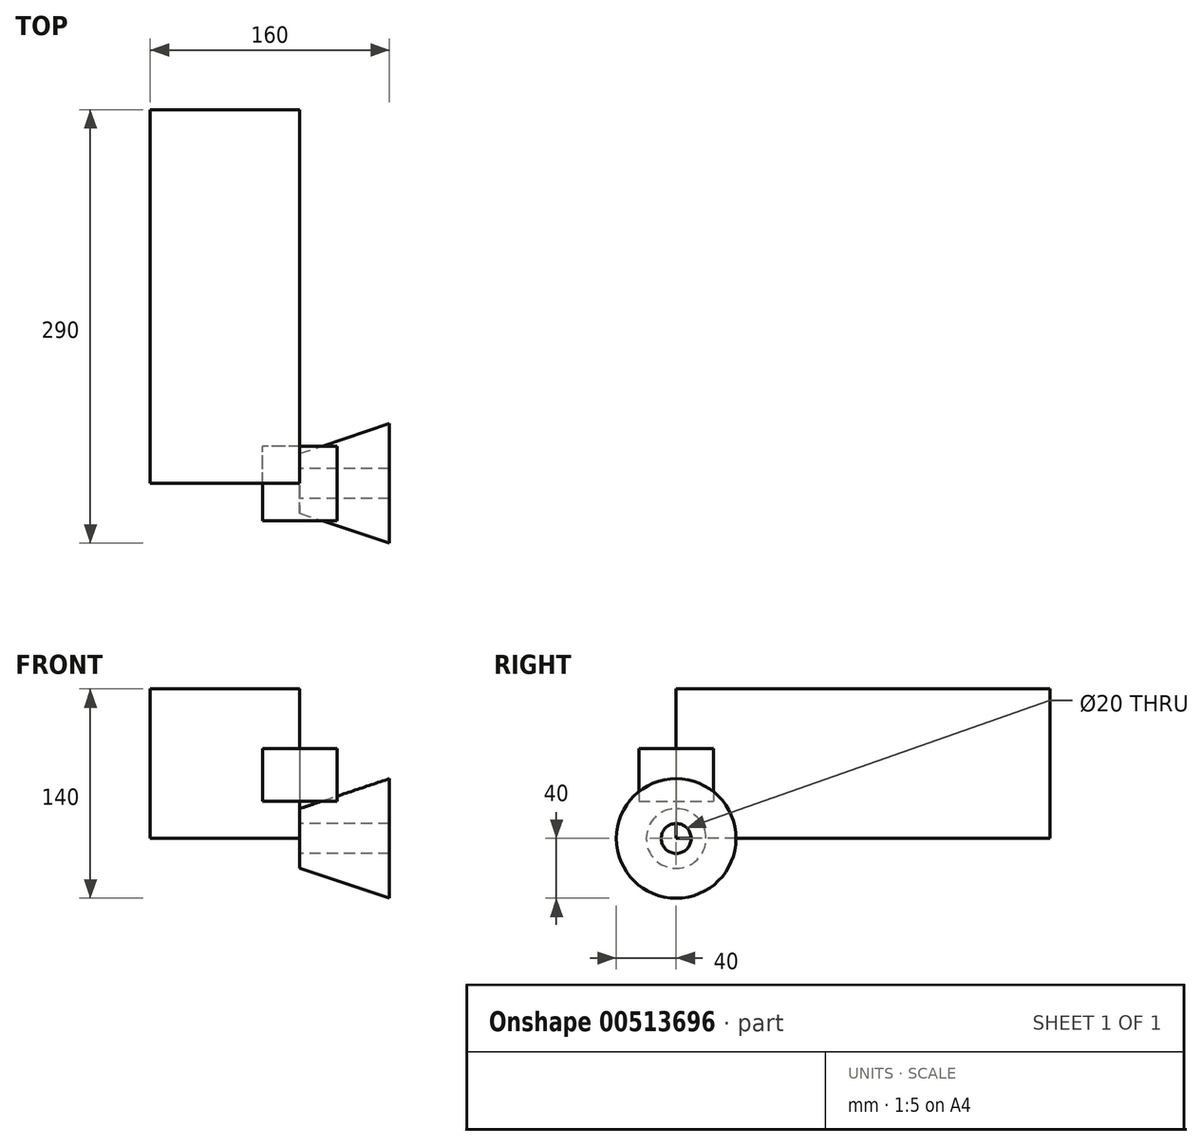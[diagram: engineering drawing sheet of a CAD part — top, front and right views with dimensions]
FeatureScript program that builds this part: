
annotation { "Feature Type Name" : "Feature", "Feature Type Description" : "" }
export const myFeature = defineFeature(function(context is Context, id is Id, definition is map)
    precondition{}
    {
        {
            var Q0;
            Q0=qCreatedBy(makeId("Top.planeOp"),FACE);
            var sketch = newSketch(context, id + "F0", { "sketchPlane" : qUnion([Q0])});
            skLineSegment(sketch, "E0.bottom", {"start": v(0, 250) * mm, "end": v(-100, 250) * mm});
            skLineSegment(sketch, "E0.top", {"start": v(0, 0) * mm, "end": v(-100, 0) * mm});
            skLineSegment(sketch, "E0.left", {"start": v(0, 250) * mm, "end": v(0, 0) * mm});
            skLineSegment(sketch, "E0.right", {"start": v(-100, 250) * mm, "end": v(-100, 0) * mm});
            skSolve(sketch);
        }
        {
            var Q0;
            Q0=makeQuery(id+"F0.imprint","IMPRINT",FACE,{"disambiguationData":[TD([[makeQuery(id+"F0.imprint","IMPRINT",EDGE,{"derivedFrom":sQuery(id+"F0.wireOp",EDGE,"E0.bottom")}),1.0]])]});
            extrude(context, id + "F1", {"entities" : qUnion([Q0]), "depth" : 100 * mm});
        }
        {
            var Q0;
            Q0=qCreatedBy(makeId("Top.planeOp"),FACE);
            var sketch = newSketch(context, id + "F2", { "sketchPlane" : qUnion([Q0])});
            skLineSegment(sketch, "E1", {"start": v(0, 20) * mm, "end": v(60, 40) * mm});
            skLineSegment(sketch, "E2", {"start": v(60, 40) * mm, "end": v(60, 10) * mm});
            skLineSegment(sketch, "E3", {"start": v(-98.63, 0) * mm, "end": v(122.44, 0) * mm, "construction": true});
            skLineSegment(sketch, "E4", {"start": v(0, 20) * mm, "end": v(0, 10) * mm});
            skLineSegment(sketch, "E5", {"start": v(0, 10) * mm, "end": v(60, 10) * mm});
            skSolve(sketch);
        }
        {
            var Q0;
            Q0=makeQuery(id+"F2.imprint","IMPRINT",FACE,{"disambiguationData":[TD([[makeQuery(id+"F2.imprint","IMPRINT",EDGE,{"derivedFrom":sQuery(id+"F2.wireOp",EDGE,"E1")}),-1.0]])]});
            var Q1;
            Q1=sQuery(id+"F2.wireOp",EDGE,"E3");
            revolve(context, id + "F3", {"entities" : qUnion([Q0]), "axis" : qUnion([Q1]), "revolveType" : RevolveType.FULL});
        }
        {
            var Q0;
            Q0=qCreatedBy(makeId("Top.planeOp"),FACE);
            var sketch = newSketch(context, id + "F4", { "sketchPlane" : qUnion([Q0])});
            skLineSegment(sketch, "E6.bottom", {"start": v(25, -25) * mm, "end": v(-25, -25) * mm});
            skLineSegment(sketch, "E6.top", {"start": v(25, 25) * mm, "end": v(-25, 25) * mm});
            skLineSegment(sketch, "E6.left", {"start": v(25, -25) * mm, "end": v(25, 25) * mm});
            skLineSegment(sketch, "E6.right", {"start": v(-25, -25) * mm, "end": v(-25, 25) * mm});
            skPoint(sketch, "E6.middle", {"position": v(0, 0) * mm});
            skSolve(sketch);
        }
        {
            var Q0;
            Q0=makeQuery(id+"F4.imprint","IMPRINT",FACE,{"disambiguationData":[TD([[makeQuery(id+"F4.imprint","IMPRINT",EDGE,{"derivedFrom":sQuery(id+"F4.wireOp",EDGE,"E6.bottom")}),-1.0]])]});
            extrude(context, id + "F5", {"entities" : qUnion([Q0]), "depth" : 60 * mm, "offsetDistance" : 25 * mm, "hasSecondDirection" : true, "secondDirectionOppositeDirection" : false, "secondDirectionDepth" : 25 * mm});
        }
    });
